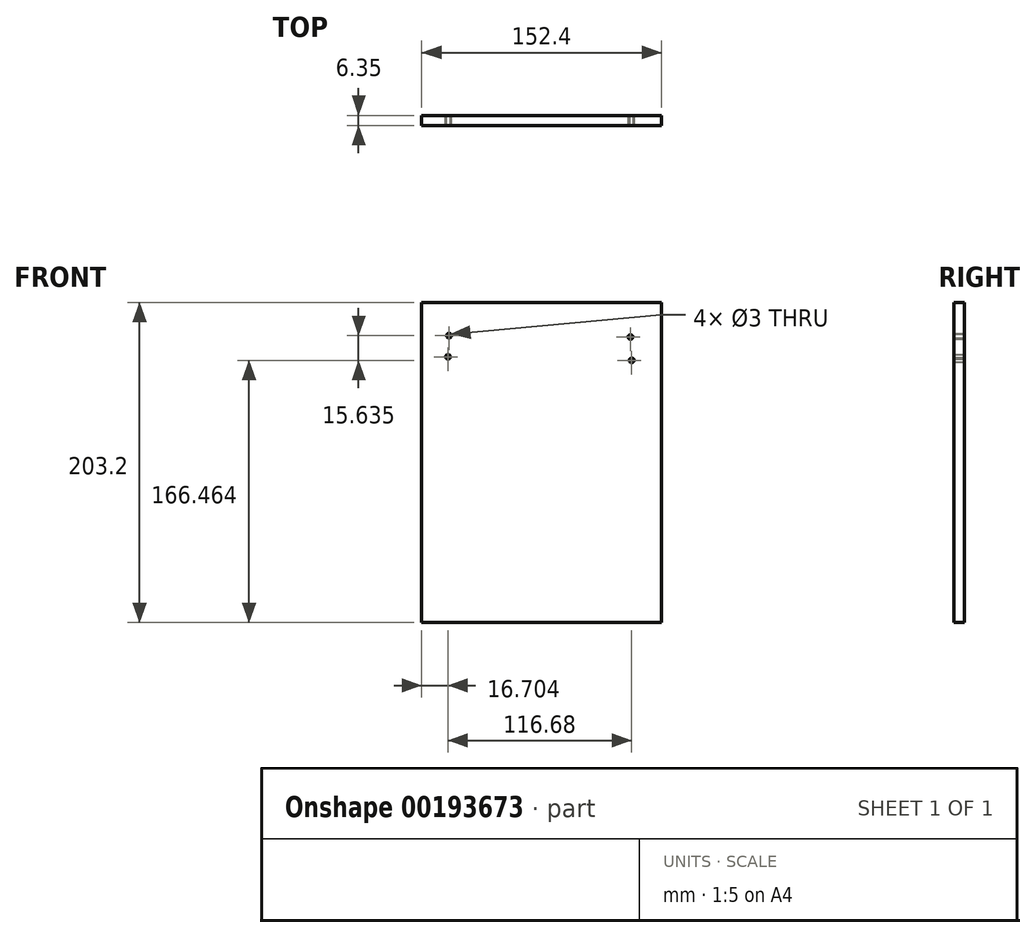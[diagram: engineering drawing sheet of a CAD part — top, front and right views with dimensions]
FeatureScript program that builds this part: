
annotation { "Feature Type Name" : "Feature", "Feature Type Description" : "" }
export const myFeature = defineFeature(function(context is Context, id is Id, definition is map)
    precondition{}
    {
        {
            var Q0;
            Q0=qCreatedBy(makeId("Front.planeOp"),FACE);
            var sketch = newSketch(context, id + "F0", { "sketchPlane" : qUnion([Q0])});
            skLineSegment(sketch, "E0.bottom", {"start": v(76.2, 101.6) * mm, "end": v(-76.2, 101.6) * mm});
            skLineSegment(sketch, "E0.top", {"start": v(76.2, -101.6) * mm, "end": v(-76.2, -101.6) * mm});
            skLineSegment(sketch, "E0.left", {"start": v(76.2, 101.6) * mm, "end": v(76.2, -101.6) * mm});
            skLineSegment(sketch, "E0.right", {"start": v(-76.2, 101.6) * mm, "end": v(-76.2, -101.6) * mm});
            skPoint(sketch, "E0.middle", {"position": v(0, 0) * mm});
            skSolve(sketch);
        }
        {
            var Q0;
            Q0=makeQuery(id+"F0.imprint","IMPRINT",FACE,{"disambiguationData":[TD([[makeQuery(id+"F0.imprint","IMPRINT",EDGE,{"derivedFrom":sQuery(id+"F0.wireOp",EDGE,"E0.bottom")}),1.0]])]});
            extrude(context, id + "F1", {"entities" : qUnion([Q0]), "depth" : 6.35 * mm});
        }
        {
            var Q0;
            Q0=qCreatedBy(makeId("Front.planeOp"),FACE);
            var sketch = newSketch(context, id + "F2", { "sketchPlane" : qUnion([Q0])});
            skCircle(sketch, "E1", {"center": v(-58.83, 80.5) * mm, "radius": 1.5 * mm});
            skSolve(sketch);
        }
        {
            var Q0;
            Q0=qCreatedBy(makeId("Front.planeOp"),FACE);
            var sketch = newSketch(context, id + "F3", { "sketchPlane" : qUnion([Q0])});
            skCircle(sketch, "E2", {"center": v(-59.5, 67.1) * mm, "radius": 1.5 * mm});
            skSolve(sketch);
        }
        {
            var Q0;
            Q0=makeQuery(id+"F2.imprint","IMPRINT",FACE,{"disambiguationData":[TD([[makeQuery(id+"F2.imprint","IMPRINT",EDGE,{"derivedFrom":sQuery(id+"F2.wireOp",EDGE,"E1")}),1.0]])]});
            var Q1;
            Q1=makeQuery(id+"F3.imprint","IMPRINT",FACE,{"disambiguationData":[TD([[makeQuery(id+"F3.imprint","IMPRINT",EDGE,{"derivedFrom":sQuery(id+"F3.wireOp",EDGE,"E2")}),1.0]])]});
            extrude(context, id + "F4", {"entities" : qUnion([Q0, Q1]), "operationType" : NewBodyOperationType.REMOVE, "depth" : 14.2 * mm});
        }
        {
            var Q0;
            Q0=qCreatedBy(makeId("Front.planeOp"),FACE);
            var sketch = newSketch(context, id + "F5", { "sketchPlane" : qUnion([Q0])});
            skCircle(sketch, "E3", {"center": v(57.18, 77.7) * mm, "radius": 1.5 * mm});
            skCircle(sketch, "E4", {"center": v(57.18, 64.52) * mm, "radius": 1.5 * mm});
            skSolve(sketch);
        }
        {
            var Q0;
            Q0 = qSketchRegion(id + "F5", true);
            extrude(context, id + "F6", {"entities" : qUnion([Q0]), "operationType" : NewBodyOperationType.REMOVE, "oppositeDirection" : true, "depth" : 25 * mm});
        }
        {
            var Q0;
            Q0=makeQuery(id+"F1.opExtrude","CAP_FACE",FACE,{"disambiguationData":[OSD([sQuery(id+"F0.wireOp",EDGE,"E0.bottom"),sQuery(id+"F0.wireOp",EDGE,"E0.top"),sQuery(id+"F0.wireOp",EDGE,"E0.left"),sQuery(id+"F0.wireOp",EDGE,"E0.right")])],"isStart":false});
            var sketch = newSketch(context, id + "F7", { "sketchPlane" : qUnion([Q0])});
            skCircle(sketch, "E5", {"center": v(56.43, 79.72) * mm, "radius": 1.5 * mm});
            skCircle(sketch, "E6", {"center": v(57.18, 64.86) * mm, "radius": 1.5 * mm});
            skSolve(sketch);
        }
        {
            var Q0;
            Q0=makeQuery(id+"F7.imprint","IMPRINT",FACE,{"disambiguationData":[TD([[makeQuery(id+"F7.imprint","IMPRINT",EDGE,{"derivedFrom":sQuery(id+"F7.wireOp",EDGE,"E5")}),1.0]])]});
            var Q1;
            Q1=makeQuery(id+"F7.imprint","IMPRINT",FACE,{"disambiguationData":[TD([[makeQuery(id+"F7.imprint","IMPRINT",EDGE,{"derivedFrom":sQuery(id+"F7.wireOp",EDGE,"E6")}),1.0]])]});
            extrude(context, id + "F8", {"entities" : qUnion([Q0, Q1]), "operationType" : NewBodyOperationType.REMOVE, "oppositeDirection" : true, "depth" : 25 * mm});
        }
    });
